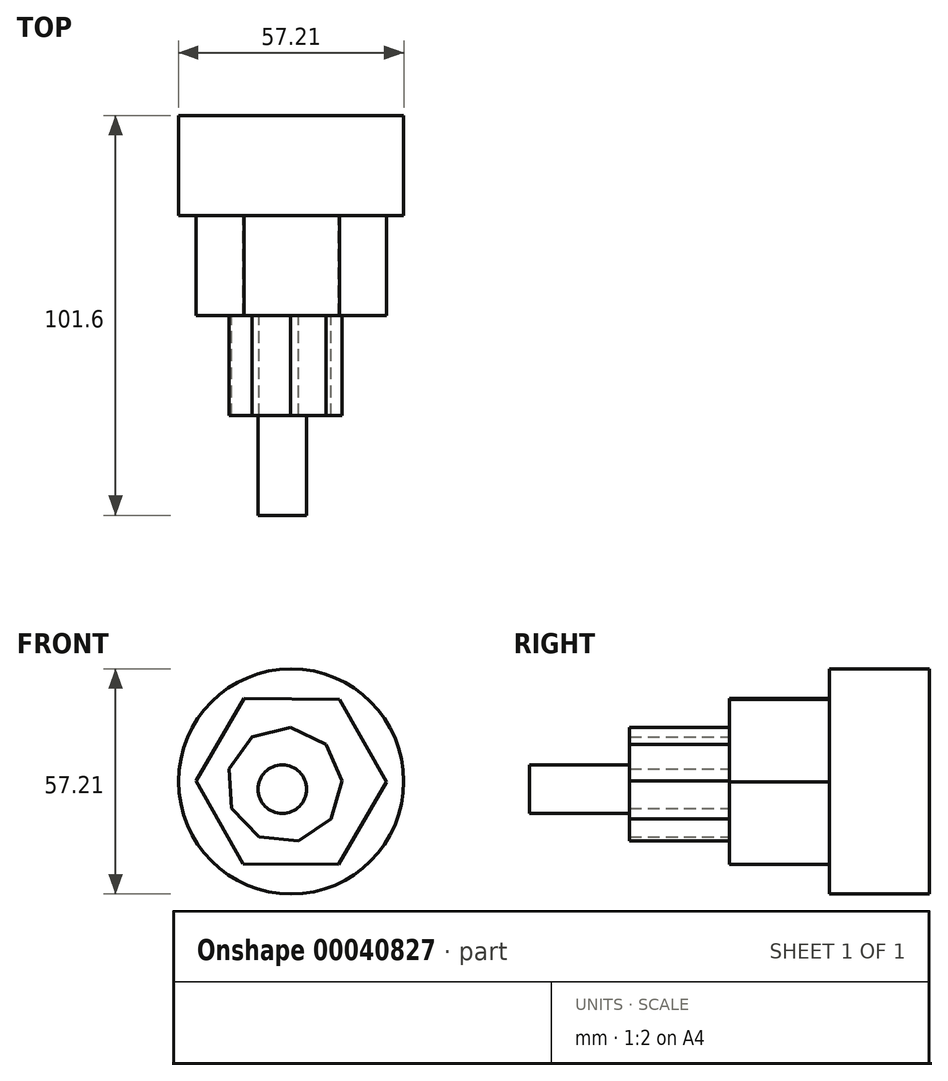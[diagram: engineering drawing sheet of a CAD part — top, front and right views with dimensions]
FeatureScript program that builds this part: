
annotation { "Feature Type Name" : "Feature", "Feature Type Description" : "" }
export const myFeature = defineFeature(function(context is Context, id is Id, definition is map)
    precondition{}
    {
        {
            var Q0;
            Q0=qCreatedBy(makeId("Front.planeOp"),FACE);
            var sketch = newSketch(context, id + "F0", { "sketchPlane" : qUnion([Q0])});
            skCircle(sketch, "E0", {"center": v(-42.04, 40.5) * mm, "radius": 28.6 * mm});
            skSolve(sketch);
        }
        {
            var Q0;
            Q0=makeQuery(id+"F0.imprint","IMPRINT",FACE,{"disambiguationData":[TD([[makeQuery(id+"F0.imprint","IMPRINT",EDGE,{"derivedFrom":sQuery(id+"F0.wireOp",EDGE,"E0")}),1.0]])]});
            extrude(context, id + "F1", {"entities" : qUnion([Q0]), "depth" : 25.4 * mm});
        }
        {
            var Q0;
            Q0=makeQuery(id+"F1.opExtrude","CAP_FACE",FACE,{"disambiguationData":[OSD([sQuery(id+"F0.wireOp",EDGE,"E0")])],"isStart":false});
            var sketch = newSketch(context, id + "F2", { "sketchPlane" : qUnion([Q0])});
            skCircle(sketch, "E1.cCircle", {"center": v(-42.04, 40.5) * mm, "radius": 20.96 * mm, "construction": true});
            skLineSegment(sketch, "E1.0", {"start": v(-29.8, 61.38) * mm, "end": v(-17.83, 40.35) * mm});
            skLineSegment(sketch, "E1.1", {"start": v(-17.83, 40.35) * mm, "end": v(-30.06, 19.46) * mm});
            skLineSegment(sketch, "E1.2", {"start": v(-30.06, 19.46) * mm, "end": v(-54.27, 19.6) * mm});
            skLineSegment(sketch, "E1.3", {"start": v(-54.27, 19.6) * mm, "end": v(-66.24, 40.64) * mm});
            skLineSegment(sketch, "E1.4", {"start": v(-66.24, 40.64) * mm, "end": v(-54, 61.53) * mm});
            skLineSegment(sketch, "E1.5", {"start": v(-54, 61.53) * mm, "end": v(-29.8, 61.38) * mm});
            skPoint(sketch, "E1.0.midPoint", {"position": v(-23.82, 50.86) * mm});
            skSolve(sketch);
        }
        {
            var Q0;
            Q0=makeQuery(id+"F2.imprint","IMPRINT",FACE,{"disambiguationData":[TD([[makeQuery(id+"F2.imprint","IMPRINT",EDGE,{"derivedFrom":sQuery(id+"F2.wireOp",EDGE,"E1.0")}),-1.0]])]});
            extrude(context, id + "F3", {"entities" : qUnion([Q0]), "operationType" : NewBodyOperationType.ADD, "depth" : 25.4 * mm});
        }
        {
            var Q0;
            Q0=makeQuery(id+"F3.opExtrude","CAP_FACE",FACE,{"disambiguationData":[OSD([sQuery(id+"F2.wireOp",EDGE,"E1.0"),sQuery(id+"F2.wireOp",EDGE,"E1.1"),sQuery(id+"F2.wireOp",EDGE,"E1.2"),sQuery(id+"F2.wireOp",EDGE,"E1.3"),sQuery(id+"F2.wireOp",EDGE,"E1.4"),sQuery(id+"F2.wireOp",EDGE,"E1.5")])],"isStart":false});
            var sketch = newSketch(context, id + "F4", { "sketchPlane" : qUnion([Q0])});
            skCircle(sketch, "E2.cCircle", {"center": v(-43.72, 39.65) * mm, "radius": 13.8 * mm, "construction": true});
            skLineSegment(sketch, "E2.0", {"start": v(-33.15, 49.85) * mm, "end": v(-29.07, 40.67) * mm});
            skLineSegment(sketch, "E2.1", {"start": v(-29.07, 40.67) * mm, "end": v(-31.84, 31.01) * mm});
            skLineSegment(sketch, "E2.2", {"start": v(-31.84, 31.01) * mm, "end": v(-40.17, 25.4) * mm});
            skLineSegment(sketch, "E2.3", {"start": v(-40.17, 25.4) * mm, "end": v(-50.16, 26.46) * mm});
            skLineSegment(sketch, "E2.4", {"start": v(-50.16, 26.46) * mm, "end": v(-57.14, 33.7) * mm});
            skLineSegment(sketch, "E2.5", {"start": v(-57.14, 33.7) * mm, "end": v(-57.83, 43.71) * mm});
            skLineSegment(sketch, "E2.6", {"start": v(-57.83, 43.71) * mm, "end": v(-51.92, 51.84) * mm});
            skLineSegment(sketch, "E2.7", {"start": v(-51.92, 51.84) * mm, "end": v(-42.17, 54.26) * mm});
            skLineSegment(sketch, "E2.8", {"start": v(-42.17, 54.26) * mm, "end": v(-33.15, 49.85) * mm});
            skPoint(sketch, "E2.0.midPoint", {"position": v(-31.1, 45.26) * mm});
            skSolve(sketch);
        }
        {
            var Q0;
            Q0=makeQuery(id+"F4.imprint","IMPRINT",FACE,{"disambiguationData":[TD([[makeQuery(id+"F4.imprint","IMPRINT",EDGE,{"derivedFrom":sQuery(id+"F4.wireOp",EDGE,"E2.0")}),-1.0]])]});
            extrude(context, id + "F5", {"entities" : qUnion([Q0]), "operationType" : NewBodyOperationType.ADD, "depth" : 25.4 * mm});
        }
        {
            var Q0;
            Q0=makeQuery(id+"F5.opExtrude","CAP_FACE",FACE,{"disambiguationData":[OSD([sQuery(id+"F4.wireOp",EDGE,"E2.0"),sQuery(id+"F4.wireOp",EDGE,"E2.1"),sQuery(id+"F4.wireOp",EDGE,"E2.2"),sQuery(id+"F4.wireOp",EDGE,"E2.3"),sQuery(id+"F4.wireOp",EDGE,"E2.4"),sQuery(id+"F4.wireOp",EDGE,"E2.5"),sQuery(id+"F4.wireOp",EDGE,"E2.6"),sQuery(id+"F4.wireOp",EDGE,"E2.7"),sQuery(id+"F4.wireOp",EDGE,"E2.8")])],"isStart":false});
            var sketch = newSketch(context, id + "F6", { "sketchPlane" : qUnion([Q0])});
            skCircle(sketch, "E3", {"center": v(-44.28, 38.53) * mm, "radius": 6.17 * mm});
            skSolve(sketch);
        }
        {
            var Q0;
            Q0=makeQuery(id+"F6.imprint","IMPRINT",FACE,{"disambiguationData":[TD([[makeQuery(id+"F6.imprint","IMPRINT",EDGE,{"derivedFrom":sQuery(id+"F6.wireOp",EDGE,"E3")}),1.0]])]});
            extrude(context, id + "F7", {"entities" : qUnion([Q0]), "operationType" : NewBodyOperationType.ADD, "depth" : 25.4 * mm});
        }
    });
